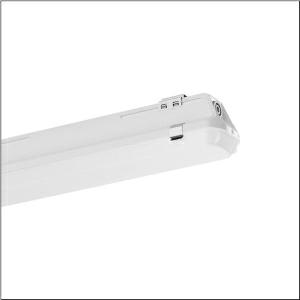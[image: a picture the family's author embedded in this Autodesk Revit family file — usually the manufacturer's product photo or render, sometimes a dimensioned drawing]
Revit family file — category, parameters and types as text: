
# Revit family: monsun_11_51fp109p440h
name_source: partatom
category: Lighting Fixtures
units: mm (PartAtom-declared; Revit-internal decimal feet)

## family parameters
Cut with Voids When Loaded = No
Host = Face
Light Source = No
Part Type = Normal
Room Calculation Point = No
Round Connector Dimension = Use Diameter
Shared = No

## types (1)
- Monsun 11 (1 x LED, 4120 lm, 22.9 W, 4000K)
    Apparent Load = 23 VA
    CIE Flux Codes = 47 77 93 94 100
    Color Rendering = 80
    Color Temperature = 4000K
    Default Elevation = 1800 mm
    Description = Monsun 11, damp-proof luminaire, chain hanger, primary optical cover: enclosure, of PMMA, light emission: direct distribution, primary light characteristic: symmetric, installation type: suspended mounting, surface-mounted, horizontal mounting, vertical mounting, LED, rated luminous flux: 4.120lm, luminous efficacy: 180lm/W, light colour: 840, colour temperature: 4000K, control gear: ON/OFF, CLOi, with terminal, 3-pole, max. 2.5mm², mains connection: 220..240V, AC, 50/60Hz, start of lifetime: 23W, end of service life: 25W, luminaire housing, of glass-fibre reinforced polyester, uncoated, bright grey, incl. chain hanger, length: 1.590mm, width: 90mm, height: 88mm, clip for enclosure, of stainless steel (V2A), ceiling mounting element, of stainless steel (V2A), chain hanger, of stainless steel (V2A), protection rating (complete): IP66, insulation class (complete): insulation class I (protective earthing), certification: CE, ENEC, VDE, UKCA, protection symbol: D, impact resistance: IK04, permissible operating ambient temperature: -35..+40°C, standard: EN 50419, EN 60598-2-1, no direct snow, no direct sun, no direct rain, for indoor or canopied outdoor use, corresponds to IFS (International Featured Standards) requirements for safety and quality in the food industry, contact your sales advisor before using the luminaires in applications with unclear chemical exposure, large temperature fluctuations or condensation-forming humidity, LABS conformity tested according to VDMA 24364:2018-05, packaging unit: 1 piece
    Height = 89 mm
    Lamp = 1 x LED
    Lamp Light Flux = 4120 lm
    Lamp Power = 22.9 W
    Lamp count = 1
    Length = 1590 mm
    Luminous efficacy = 180 lm/W
    Manufacturer = Siteco
    ModVariant = No
    Model = 51FP109P440H
    Mounting Place = Ceiling
    Mounting Type = Surface mounted
    Number of Poles = 1
    OnlyDefault = Yes
    Power Factor = 1
    Product Name = Monsun 11
    Product group = damp-proof luminaire
    ProductGroupID = 300
    Protection Class = Protection class I
    Protection Degree = IP 66
    RLX_Detail_Level = 1
    RLX_Emergency_Light_Flux = 0 lm
    RLX_Emergency_Type = 0
    RLX_Emergency_Type_DB = No
    RlxData = <blob elided: 88293 chars, md5=eea93cc0>
    Socket = socket
    Standby Power = 0 W
    System Light Flux = 4120 lm
    System Power = 23 W
    Type Comments = Product without accessories
    Type Image = l_1349237.jpg
    URL = http://relux.com
    VarID = ---
    Voltage = 0 V
    Weight = 0.00 kg
    Width = 90 mm

## geometry (parser evidence)
native form markers: Blend x4, Sweep x13
no freeform markers — native parametric forms only
